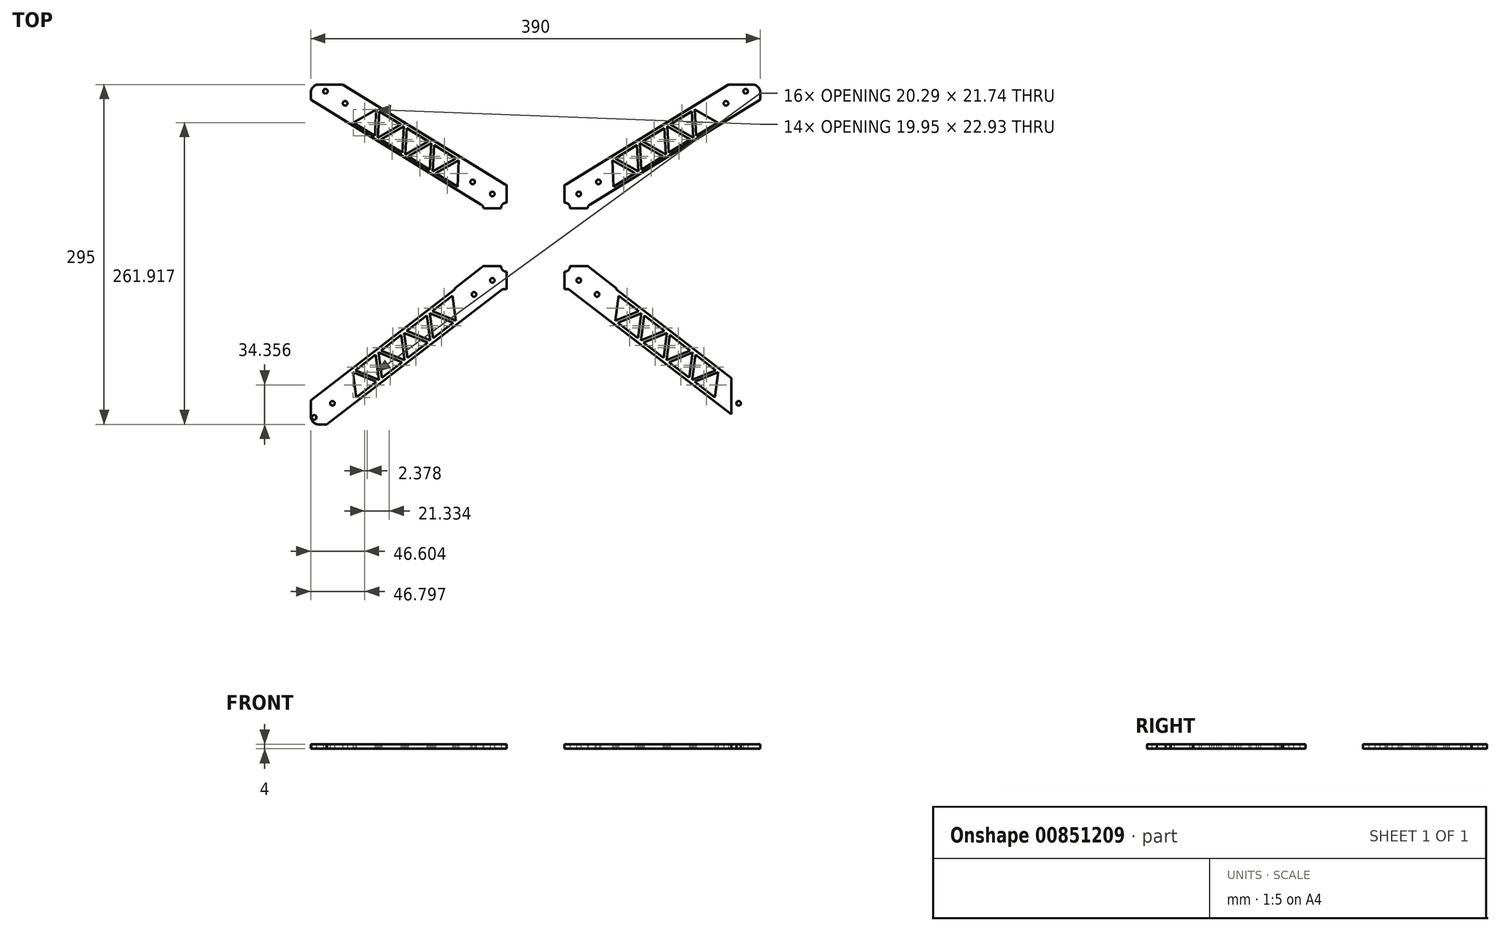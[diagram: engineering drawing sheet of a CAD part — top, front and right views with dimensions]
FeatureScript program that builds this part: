
annotation { "Feature Type Name" : "Feature", "Feature Type Description" : "" }
export const myFeature = defineFeature(function(context is Context, id is Id, definition is map)
    precondition{}
    {
        {
            var Q0;
            Q0=qCreatedBy(makeId("Top.planeOp"),FACE);
            var sketch = newSketch(context, id + "F0", { "sketchPlane" : qUnion([Q0])});
            skLineSegment(sketch, "E0.bottom", {"start": v(-37.5, -37.5) * mm, "end": v(37.5, -37.5) * mm, "construction": true});
            skLineSegment(sketch, "E0.top", {"start": v(-37.5, 37.5) * mm, "end": v(37.5, 37.5) * mm, "construction": true});
            skLineSegment(sketch, "E0.left", {"start": v(-37.5, -37.5) * mm, "end": v(-37.5, 37.5) * mm, "construction": true});
            skLineSegment(sketch, "E0.right", {"start": v(37.5, -37.5) * mm, "end": v(37.5, 37.5) * mm, "construction": true});
            skPoint(sketch, "E0.middle", {"position": v(0, 0) * mm});
            skCircle(sketch, "E1", {"center": v(-37.5, 37.5) * mm, "radius": 2 * mm});
            skCircle(sketch, "E2", {"center": v(37.5, 37.5) * mm, "radius": 2 * mm});
            skCircle(sketch, "E3", {"center": v(37.5, -37.5) * mm, "radius": 2 * mm});
            skCircle(sketch, "E4", {"center": v(-37.5, -37.5) * mm, "radius": 2 * mm});
            skLineSegment(sketch, "E5.bottom", {"start": v(25, -30) * mm, "end": v(-25, -30) * mm});
            skLineSegment(sketch, "E5.top", {"start": v(25, 30) * mm, "end": v(-25, 30) * mm});
            skLineSegment(sketch, "E5.left", {"start": v(30, -25) * mm, "end": v(30, 25) * mm});
            skLineSegment(sketch, "E5.right", {"start": v(-30, -25) * mm, "end": v(-30, 25) * mm});
            skLineSegment(sketch, "E6.bottom", {"start": v(-23.58, 45) * mm, "end": v(-7.48, 45) * mm});
            skLineSegment(sketch, "E6.left", {"start": v(-45, 24.13) * mm, "end": v(-45, -22.54) * mm});
            skLineSegment(sketch, "E6.right", {"start": v(45, 40) * mm, "end": v(45, -40) * mm});
            skPoint(sketch, "E7.visualSharp", {"position": v(-30, 30) * mm});
            skArc(sketch, "E7.filletArc", {"start": v(-25, 30) * mm, "mid": v(-28.54, 28.54) * mm, "end": v(-30, 25) * mm});
            skPoint(sketch, "E8.visualSharp", {"position": v(30, 30) * mm});
            skArc(sketch, "E8.filletArc", {"start": v(30, 25) * mm, "mid": v(28.54, 28.54) * mm, "end": v(25, 30) * mm});
            skPoint(sketch, "E9.visualSharp", {"position": v(30, -30) * mm});
            skArc(sketch, "E9.filletArc", {"start": v(25, -30) * mm, "mid": v(28.54, -28.54) * mm, "end": v(30, -25) * mm});
            skPoint(sketch, "E10.visualSharp", {"position": v(-30, -30) * mm});
            skArc(sketch, "E10.filletArc", {"start": v(-30, -25) * mm, "mid": v(-28.54, -28.54) * mm, "end": v(-25, -30) * mm});
            skPoint(sketch, "E11.visualSharp", {"position": v(45, 45) * mm});
            skArc(sketch, "E11.filletArc", {"start": v(45, 40) * mm, "mid": v(43.54, 43.54) * mm, "end": v(40, 45) * mm});
            skPoint(sketch, "E12.visualSharp", {"position": v(-45, 45) * mm});
            skPoint(sketch, "E13.visualSharp", {"position": v(45, -45) * mm});
            skArc(sketch, "E13.filletArc", {"start": v(40, -45) * mm, "mid": v(43.54, -43.54) * mm, "end": v(45, -40) * mm});
            skPoint(sketch, "E14.visualSharp", {"position": v(-45, -45) * mm});
            skLineSegment(sketch, "E15", {"start": v(-37.5, -37.5) * mm, "end": v(-37.5, -162.5) * mm, "construction": true});
            skLineSegment(sketch, "E16", {"start": v(0, 0) * mm, "end": v(0, -162.5) * mm, "construction": true});
            skLineSegment(sketch, "E17", {"start": v(0, -162.5) * mm, "end": v(200, -162.5) * mm});
            skLineSegment(sketch, "E18", {"start": v(200, -162.5) * mm, "end": v(200, 137.5) * mm, "construction": true});
            skLineSegment(sketch, "E19", {"start": v(200, 137.5) * mm, "end": v(-200, 137.5) * mm, "construction": true});
            skLineSegment(sketch, "E20", {"start": v(-200, 137.5) * mm, "end": v(-200, -162.5) * mm, "construction": true});
            skLineSegment(sketch, "E21", {"start": v(-200, -162.5) * mm, "end": v(0, -162.5) * mm, "construction": true});
            skLineSegment(sketch, "E22", {"start": v(-37.5, 37.5) * mm, "end": v(-200, 137.5) * mm, "construction": true});
            skLineSegment(sketch, "E23", {"start": v(-26.2, 45.74) * mm, "end": v(-56.68, 64.5) * mm});
            skLineSegment(sketch, "E24", {"start": v(-56.68, 64.5) * mm, "end": v(-63.46, 53.47) * mm});
            skLineSegment(sketch, "E25.MirrorCS", {"start": v(-47.38, 28.39) * mm, "end": v(-70.24, 42.45) * mm});
            skLineSegment(sketch, "E26.MirrorCS", {"start": v(-70.24, 42.45) * mm, "end": v(-63.46, 53.47) * mm});
            skPoint(sketch, "E27.orphan", {"position": v(-38.56, 22.96) * mm});
            skPoint(sketch, "E28.visualSharp", {"position": v(-45, 26.92) * mm});
            skArc(sketch, "E28.filletArc", {"start": v(-45, 24.13) * mm, "mid": v(-45.64, 26.57) * mm, "end": v(-47.38, 28.39) * mm});
            skPoint(sketch, "E29.visualSharp", {"position": v(-25, 45) * mm});
            skArc(sketch, "E29.filletArc", {"start": v(-26.2, 45.74) * mm, "mid": v(-24.95, 45.19) * mm, "end": v(-23.58, 45) * mm});
            skLineSegment(sketch, "E30", {"start": v(-37.5, 37.5) * mm, "end": v(-39.84, 33.7) * mm, "construction": true});
            skLineSegment(sketch, "E31", {"start": v(-39.84, 33.7) * mm, "end": v(-56.88, 44.17) * mm, "construction": true});
            skLineSegment(sketch, "E32", {"start": v(-56.88, 44.17) * mm, "end": v(-54.53, 47.98) * mm, "construction": true});
            skCircle(sketch, "E33", {"center": v(-54.53, 47.98) * mm, "radius": 2 * mm});
            skLineSegment(sketch, "E34.bottom", {"start": v(-200, 137.5) * mm, "end": v(-151.5, 137.5) * mm});
            skLineSegment(sketch, "E34.top", {"start": v(-200, 107.5) * mm, "end": v(-151.5, 107.5) * mm});
            skLineSegment(sketch, "E34.left", {"start": v(-200, 137.5) * mm, "end": v(-200, 107.5) * mm});
            skLineSegment(sketch, "E34.right", {"start": v(-151.5, 137.5) * mm, "end": v(-151.5, 107.5) * mm});
            skLineSegment(sketch, "E35.bottom", {"start": v(-151.5, 107.5) * mm, "end": v(-195, 107.5) * mm});
            skLineSegment(sketch, "E35.top", {"start": v(-151.5, 132.5) * mm, "end": v(-195, 132.5) * mm});
            skLineSegment(sketch, "E35.left", {"start": v(-151.5, 107.5) * mm, "end": v(-151.5, 132.5) * mm});
            skLineSegment(sketch, "E35.right", {"start": v(-195, 107.5) * mm, "end": v(-195, 132.5) * mm});
            skLineSegment(sketch, "E36", {"start": v(-56.88, 44.17) * mm, "end": v(-167.6, 112.3) * mm, "construction": true});
            skLineSegment(sketch, "E37", {"start": v(-167.6, 112.3) * mm, "end": v(-165.25, 116.11) * mm, "construction": true});
            skCircle(sketch, "E38", {"center": v(-165.25, 116.11) * mm, "radius": 2 * mm});
            skLineSegment(sketch, "E39", {"start": v(-167.6, 112.3) * mm, "end": v(-184.63, 122.79) * mm, "construction": true});
            skLineSegment(sketch, "E40", {"start": v(-184.63, 122.79) * mm, "end": v(-182.28, 126.6) * mm, "construction": true});
            skCircle(sketch, "E41", {"center": v(-182.28, 126.6) * mm, "radius": 2 * mm});
            skLineSegment(sketch, "E42", {"start": v(0, -34.68) * mm, "end": v(15, -34.68) * mm, "construction": true});
            skCircle(sketch, "E43", {"center": v(15, -37.5) * mm, "radius": 2.2 * mm});
            skLineSegment(sketch, "E44", {"start": v(0, 0) * mm, "end": v(-16.78, 0) * mm, "construction": true});
            skLineSegment(sketch, "E45", {"start": v(0, 0) * mm, "end": v(-10.77, -10.77) * mm, "construction": true});
            skCircle(sketch, "E46.MirrorC", {"center": v(-15, -37.5) * mm, "radius": 2.2 * mm});
            skCircle(sketch, "E47.MirrorC", {"center": v(-37.5, 15) * mm, "radius": 2.2 * mm});
            skCircle(sketch, "E48.MirrorC", {"center": v(-37.5, -15) * mm, "radius": 2.2 * mm});
            skCircle(sketch, "E49.MirrorC", {"center": v(-15, 37.5) * mm, "radius": 2.2 * mm});
            skCircle(sketch, "E50.MirrorC", {"center": v(15, 37.5) * mm, "radius": 2.2 * mm});
            skCircle(sketch, "E51.MirrorC", {"center": v(37.5, -15) * mm, "radius": 2.2 * mm});
            skCircle(sketch, "E52.MirrorC", {"center": v(37.5, 15) * mm, "radius": 2.2 * mm});
            skLineSegment(sketch, "E53", {"start": v(0, 0) * mm, "end": v(-200, 0) * mm, "construction": true});
            skLineSegment(sketch, "E54", {"start": v(0, 0) * mm, "end": v(0, 137.5) * mm, "construction": true});
            skLineSegment(sketch, "E55.MirrorCS", {"start": v(167.6, 112.3) * mm, "end": v(165.25, 116.11) * mm, "construction": true});
            skCircle(sketch, "E56.MirrorC", {"center": v(165.25, 116.11) * mm, "radius": 2 * mm});
            skCircle(sketch, "E57.MirrorC", {"center": v(182.28, 126.6) * mm, "radius": 2 * mm});
            skLineSegment(sketch, "E58.MirrorCS", {"start": v(184.63, 122.79) * mm, "end": v(182.28, 126.6) * mm, "construction": true});
            skLineSegment(sketch, "E59.MirrorCS", {"start": v(151.5, 107.5) * mm, "end": v(151.5, 132.5) * mm});
            skLineSegment(sketch, "E60.MirrorCS", {"start": v(151.5, 107.5) * mm, "end": v(195, 107.5) * mm});
            skLineSegment(sketch, "E61.MirrorCS", {"start": v(151.5, 132.5) * mm, "end": v(195, 132.5) * mm});
            skLineSegment(sketch, "E62.MirrorCS", {"start": v(200, 137.5) * mm, "end": v(151.5, 137.5) * mm});
            skLineSegment(sketch, "E63.MirrorCS", {"start": v(151.5, 137.5) * mm, "end": v(151.5, 107.5) * mm});
            skLineSegment(sketch, "E64.MirrorCS", {"start": v(195, 107.5) * mm, "end": v(195, 132.5) * mm});
            skLineSegment(sketch, "E65.MirrorCS", {"start": v(167.6, 112.3) * mm, "end": v(184.63, 122.79) * mm, "construction": true});
            skLineSegment(sketch, "E66.MirrorCS", {"start": v(200, 107.5) * mm, "end": v(151.5, 107.5) * mm});
            skLineSegment(sketch, "E67.MirrorCS", {"start": v(200, 137.5) * mm, "end": v(200, 107.5) * mm});
            skLineSegment(sketch, "E68", {"start": v(-37.5, -37.5) * mm, "end": v(-200, -162.5) * mm, "construction": true});
            skLineSegment(sketch, "E69.bottom", {"start": v(-200, -162.5) * mm, "end": v(-170, -162.5) * mm});
            skLineSegment(sketch, "E69.top", {"start": v(-200, -114) * mm, "end": v(-170, -114) * mm});
            skLineSegment(sketch, "E69.left", {"start": v(-200, -162.5) * mm, "end": v(-200, -114) * mm});
            skLineSegment(sketch, "E69.right", {"start": v(-170, -162.5) * mm, "end": v(-170, -114) * mm});
            skLineSegment(sketch, "E70", {"start": v(-46.95, -26.5) * mm, "end": v(-70.24, -44.42) * mm});
            skLineSegment(sketch, "E71", {"start": v(-70.24, 42.45) * mm, "end": v(-70.24, -45.57) * mm, "construction": true});
            skLineSegment(sketch, "E72", {"start": v(-70.24, -44.42) * mm, "end": v(-54.47, -64.92) * mm});
            skLineSegment(sketch, "E73", {"start": v(-54.47, -64.92) * mm, "end": v(-29.92, -46.04) * mm});
            skLineSegment(sketch, "E74", {"start": v(-37.5, -37.5) * mm, "end": v(-40.46, -33.65) * mm, "construction": true});
            skLineSegment(sketch, "E75", {"start": v(-40.46, -33.65) * mm, "end": v(-56.31, -45.85) * mm, "construction": true});
            skLineSegment(sketch, "E76", {"start": v(-56.31, -45.85) * mm, "end": v(-53.35, -49.7) * mm, "construction": true});
            skCircle(sketch, "E77", {"center": v(-53.35, -49.7) * mm, "radius": 2 * mm});
            skLineSegment(sketch, "E78", {"start": v(-56.31, -45.85) * mm, "end": v(-179.17, -140.35) * mm, "construction": true});
            skLineSegment(sketch, "E79", {"start": v(-179.17, -140.35) * mm, "end": v(-176.2, -144.2) * mm, "construction": true});
            skCircle(sketch, "E80", {"center": v(-176.2, -144.2) * mm, "radius": 2 * mm});
            skLineSegment(sketch, "E81", {"start": v(-179.17, -140.35) * mm, "end": v(-195.02, -152.55) * mm, "construction": true});
            skLineSegment(sketch, "E82", {"start": v(-195.02, -152.55) * mm, "end": v(-192.06, -156.4) * mm, "construction": true});
            skCircle(sketch, "E83", {"center": v(-192.06, -156.4) * mm, "radius": 2 * mm});
            skLineSegment(sketch, "E84.bottom", {"start": v(-170, -114) * mm, "end": v(-195, -114) * mm});
            skLineSegment(sketch, "E84.top", {"start": v(-170, -162.5) * mm, "end": v(-195, -162.5) * mm});
            skLineSegment(sketch, "E84.left", {"start": v(-170, -114) * mm, "end": v(-170, -162.5) * mm});
            skLineSegment(sketch, "E84.right", {"start": v(-195, -114) * mm, "end": v(-195, -162.5) * mm});
            skLineSegment(sketch, "E85.MirrorCS", {"start": v(179.17, -140.35) * mm, "end": v(176.2, -144.2) * mm, "construction": true});
            skCircle(sketch, "E86.MirrorC", {"center": v(176.2, -144.2) * mm, "radius": 2 * mm});
            skCircle(sketch, "E87.MirrorC", {"center": v(192.06, -156.4) * mm, "radius": 2 * mm});
            skLineSegment(sketch, "E88.MirrorCS", {"start": v(195.02, -152.55) * mm, "end": v(192.06, -156.4) * mm, "construction": true});
            skLineSegment(sketch, "E89.MirrorCS", {"start": v(170, -162.5) * mm, "end": v(170, -114) * mm});
            skLineSegment(sketch, "E90.MirrorCS", {"start": v(179.17, -140.35) * mm, "end": v(195.02, -152.55) * mm, "construction": true});
            skLineSegment(sketch, "E91.MirrorCS", {"start": v(170, -162.5) * mm, "end": v(195, -162.5) * mm});
            skLineSegment(sketch, "E92.MirrorCS", {"start": v(200, -114) * mm, "end": v(170, -114) * mm});
            skLineSegment(sketch, "E93.MirrorCS", {"start": v(170, -114) * mm, "end": v(195, -114) * mm});
            skLineSegment(sketch, "E94.MirrorCS", {"start": v(200, -162.5) * mm, "end": v(200, -114) * mm});
            skLineSegment(sketch, "E95.MirrorCS", {"start": v(170, -114) * mm, "end": v(170, -162.5) * mm});
            skLineSegment(sketch, "E96.MirrorCS", {"start": v(200, -162.5) * mm, "end": v(170, -162.5) * mm});
            skLineSegment(sketch, "E97.MirrorCS", {"start": v(195, -114) * mm, "end": v(195, -162.5) * mm});
            skLineSegment(sketch, "E98.trimOffspring", {"start": v(-26.87, -45) * mm, "end": v(40, -45) * mm});
            skPoint(sketch, "E99.visualSharp", {"position": v(-45, -25) * mm});
            skArc(sketch, "E99.filletArc", {"start": v(-46.95, -26.5) * mm, "mid": v(-45.51, -24.75) * mm, "end": v(-45, -22.54) * mm});
            skPoint(sketch, "E100.visualSharp", {"position": v(-28.57, -45) * mm});
            skArc(sketch, "E100.filletArc", {"start": v(-26.87, -45) * mm, "mid": v(-28.48, -45.27) * mm, "end": v(-29.92, -46.04) * mm});
            skPoint(sketch, "E101.MirrorP", {"position": v(28.57, -45) * mm});
            skArc(sketch, "E102.MirrorCS", {"start": v(26.87, -45) * mm, "mid": v(28.48, -45.27) * mm, "end": v(29.92, -46.04) * mm});
            skLineSegment(sketch, "E103.MirrorCS", {"start": v(54.47, -64.92) * mm, "end": v(29.92, -46.04) * mm});
            skArc(sketch, "E104.MirrorCS", {"start": v(46.95, -26.5) * mm, "mid": v(45.51, -24.75) * mm, "end": v(45, -22.54) * mm});
            skLineSegment(sketch, "E105.MirrorCS", {"start": v(46.95, -26.5) * mm, "end": v(70.24, -44.42) * mm});
            skCircle(sketch, "E106.MirrorC", {"center": v(53.35, -49.7) * mm, "radius": 2 * mm});
            skLineSegment(sketch, "E107.MirrorCS", {"start": v(70.24, -44.42) * mm, "end": v(54.47, -64.92) * mm});
            skArc(sketch, "E108.MirrorCS", {"start": v(26.2, 45.74) * mm, "mid": v(24.95, 45.19) * mm, "end": v(23.58, 45) * mm});
            skLineSegment(sketch, "E109.MirrorCS", {"start": v(26.2, 45.74) * mm, "end": v(56.68, 64.5) * mm});
            skArc(sketch, "E110.MirrorCS", {"start": v(45, 24.13) * mm, "mid": v(45.64, 26.57) * mm, "end": v(47.38, 28.39) * mm});
            skLineSegment(sketch, "E111.MirrorCS", {"start": v(47.38, 28.39) * mm, "end": v(70.24, 42.45) * mm});
            skLineSegment(sketch, "E112.MirrorCS", {"start": v(56.68, 64.5) * mm, "end": v(63.46, 53.47) * mm});
            skCircle(sketch, "E113.MirrorC", {"center": v(54.53, 47.98) * mm, "radius": 2 * mm});
            skLineSegment(sketch, "E114.MirrorCS", {"start": v(70.24, 42.45) * mm, "end": v(63.46, 53.47) * mm});
            skArc(sketch, "E115", {"start": v(3.33, 47.22) * mm, "mid": v(0, 49) * mm, "end": v(-3.33, 47.22) * mm});
            skLineSegment(sketch, "E116.trimOffspring", {"start": v(7.48, 45) * mm, "end": v(40, 45) * mm});
            skPoint(sketch, "E117.visualSharp", {"position": v(4, 45) * mm});
            skArc(sketch, "E117.filletArc", {"start": v(3.33, 47.22) * mm, "mid": v(5.13, 45.6) * mm, "end": v(7.48, 45) * mm});
            skPoint(sketch, "E118.visualSharp", {"position": v(-4, 45) * mm});
            skArc(sketch, "E118.filletArc", {"start": v(-7.48, 45) * mm, "mid": v(-5.13, 45.6) * mm, "end": v(-3.33, 47.22) * mm});
            skLineSegment(sketch, "E119", {"start": v(-165.25, 116.11) * mm, "end": v(-161.58, 122.08) * mm, "construction": true});
            skLineSegment(sketch, "E120", {"start": v(-161.58, 122.08) * mm, "end": v(-151.5, 115.87) * mm});
            skLineSegment(sketch, "E121", {"start": v(-161.58, 122.08) * mm, "end": v(-178.52, 132.5) * mm});
            skLineSegment(sketch, "E122.MirrorCS", {"start": v(-30.16, 49.42) * mm, "end": v(-192.66, 149.42) * mm, "construction": true});
            skLineSegment(sketch, "E123.MirrorCS", {"start": v(-168.92, 110.15) * mm, "end": v(-185.86, 120.58) * mm});
            skLineSegment(sketch, "E124", {"start": v(-168.92, 110.15) * mm, "end": v(-164.6, 107.5) * mm});
            skLineSegment(sketch, "E125", {"start": v(-185.86, 120.58) * mm, "end": v(-195, 126.2) * mm});
            skLineSegment(sketch, "E126", {"start": v(-164.6, 107.5) * mm, "end": v(-157.27, 119.42) * mm});
            skLineSegment(sketch, "E127", {"start": v(-70.24, 42.45) * mm, "end": v(-195, 119.23) * mm});
            skLineSegment(sketch, "E128", {"start": v(-56.68, 64.5) * mm, "end": v(-167.19, 132.5) * mm});
            skLineSegment(sketch, "E129", {"start": v(-30, 25) * mm, "end": v(-45.08, 25) * mm});
            skLineSegment(sketch, "E130", {"start": v(-25, 30) * mm, "end": v(-25, 45.2) * mm});
            skLineSegment(sketch, "E131", {"start": v(-159.49, 97.38) * mm, "end": v(-158.18, 99.5) * mm, "construction": true});
            skLineSegment(sketch, "E132", {"start": v(-158.18, 99.5) * mm, "end": v(-139.4, 87.95) * mm});
            skLineSegment(sketch, "E133", {"start": v(-148.79, 93.73) * mm, "end": v(-138.23, 110.88) * mm, "construction": true});
            skLineSegment(sketch, "E134", {"start": v(-139.4, 87.95) * mm, "end": v(-138.23, 110.88) * mm});
            skLineSegment(sketch, "E135", {"start": v(-138.23, 110.88) * mm, "end": v(-158.18, 99.5) * mm});
            skLineSegment(sketch, "E136", {"start": v(-139.4, 87.95) * mm, "end": v(-136.84, 86.38) * mm, "construction": true});
            skLineSegment(sketch, "E137", {"start": v(-138.23, 110.88) * mm, "end": v(-135.67, 109.31) * mm, "construction": true});
            skLineSegment(sketch, "E138", {"start": v(-136.84, 86.38) * mm, "end": v(-135.67, 109.31) * mm});
            skLineSegment(sketch, "E139", {"start": v(-135.67, 109.31) * mm, "end": v(-116.9, 97.76) * mm});
            skLineSegment(sketch, "E140", {"start": v(-136.84, 86.38) * mm, "end": v(-116.9, 97.76) * mm});
            skLineSegment(sketch, "E141", {"start": v(-116.9, 97.76) * mm, "end": v(-114.34, 96.18) * mm, "construction": true});
            skLineSegment(sketch, "E142", {"start": v(-114.34, 96.18) * mm, "end": v(-116.1, 93.32) * mm, "construction": true});
            skLineSegment(sketch, "E143.MirrorCS", {"start": v(-112.95, 71.68) * mm, "end": v(-111.79, 94.61) * mm});
            skLineSegment(sketch, "E144.MirrorCS", {"start": v(-93, 83.05) * mm, "end": v(-111.79, 94.61) * mm});
            skLineSegment(sketch, "E145.MirrorCS", {"start": v(-112.95, 71.68) * mm, "end": v(-93, 83.05) * mm});
            skLineSegment(sketch, "E146.MirrorCS", {"start": v(-110.4, 70.1) * mm, "end": v(-90.45, 81.48) * mm});
            skLineSegment(sketch, "E147.MirrorCS", {"start": v(-91.62, 58.55) * mm, "end": v(-110.4, 70.1) * mm});
            skLineSegment(sketch, "E148.MirrorCS", {"start": v(-90.45, 81.48) * mm, "end": v(-91.62, 58.55) * mm});
            skLineSegment(sketch, "E149", {"start": v(-138.12, 87.16) * mm, "end": v(-138.8, 86.07) * mm, "construction": true});
            skLineSegment(sketch, "E150", {"start": v(-136.84, 86.38) * mm, "end": v(-139.31, 82.36) * mm, "construction": true});
            skLineSegment(sketch, "E151.MirrorCS", {"start": v(-134.29, 84.8) * mm, "end": v(-114.34, 96.18) * mm});
            skLineSegment(sketch, "E152.MirrorCS", {"start": v(-114.34, 96.18) * mm, "end": v(-115.5, 73.25) * mm});
            skLineSegment(sketch, "E153.MirrorCS", {"start": v(-115.5, 73.25) * mm, "end": v(-134.29, 84.8) * mm});
            skLineSegment(sketch, "E154", {"start": v(-101, 64.33) * mm, "end": v(-103.36, 60.5) * mm, "construction": true});
            skLineSegment(sketch, "E155.MirrorCS", {"start": v(-89.06, 56.97) * mm, "end": v(-69.12, 68.35) * mm});
            skLineSegment(sketch, "E156.MirrorCS", {"start": v(-89.06, 56.97) * mm, "end": v(-87.9, 79.9) * mm});
            skLineSegment(sketch, "E157.MirrorCS", {"start": v(-87.9, 79.9) * mm, "end": v(-69.12, 68.35) * mm});
            skLineSegment(sketch, "E158", {"start": v(-89.06, 56.97) * mm, "end": v(-91.75, 52.6) * mm, "construction": true});
            skLineSegment(sketch, "E159.MirrorCS", {"start": v(-66.56, 66.78) * mm, "end": v(-86.5, 55.4) * mm});
            skLineSegment(sketch, "E160.MirrorCS", {"start": v(-67.73, 43.85) * mm, "end": v(-66.56, 66.78) * mm});
            skLineSegment(sketch, "E161.MirrorCS", {"start": v(-86.5, 55.4) * mm, "end": v(-67.73, 43.85) * mm});
            skLineSegment(sketch, "E162", {"start": v(-54.47, -64.92) * mm, "end": v(-190.45, -169.52) * mm});
            skLineSegment(sketch, "E163", {"start": v(-70.24, -45.57) * mm, "end": v(-195, -141.54) * mm});
            skPoint(sketch, "E163.endSnap0", {"position": v(-195, -138.25) * mm});
            skLineSegment(sketch, "E164", {"start": v(-73.84, -48.34) * mm, "end": v(-72.01, -50.71) * mm, "construction": true});
            skLineSegment(sketch, "E165", {"start": v(-72.01, -50.71) * mm, "end": v(-89.48, -64.15) * mm});
            skLineSegment(sketch, "E166", {"start": v(-80.75, -57.43) * mm, "end": v(-69.2, -72.45) * mm, "construction": true});
            skLineSegment(sketch, "E167", {"start": v(-72.01, -50.71) * mm, "end": v(-69.2, -72.45) * mm});
            skLineSegment(sketch, "E168", {"start": v(-89.48, -64.15) * mm, "end": v(-69.2, -72.45) * mm});
            skLineSegment(sketch, "E169", {"start": v(-89.48, -64.15) * mm, "end": v(-91.86, -65.98) * mm, "construction": true});
            skLineSegment(sketch, "E170", {"start": v(-69.2, -72.45) * mm, "end": v(-71.57, -74.28) * mm, "construction": true});
            skLineSegment(sketch, "E171", {"start": v(-91.86, -65.98) * mm, "end": v(-71.57, -74.28) * mm});
            skLineSegment(sketch, "E172", {"start": v(-71.57, -74.28) * mm, "end": v(-89.04, -87.72) * mm});
            skLineSegment(sketch, "E173", {"start": v(-91.86, -65.98) * mm, "end": v(-89.04, -87.72) * mm});
            skLineSegment(sketch, "E174", {"start": v(-80.3, -81) * mm, "end": v(-78.47, -83.39) * mm, "construction": true});
            skLineSegment(sketch, "E175.MirrorCS", {"start": v(-94.24, -67.81) * mm, "end": v(-91.42, -89.55) * mm});
            skLineSegment(sketch, "E176.MirrorCS", {"start": v(-111.7, -81.25) * mm, "end": v(-94.24, -67.81) * mm});
            skLineSegment(sketch, "E177.MirrorCS", {"start": v(-111.7, -81.25) * mm, "end": v(-91.42, -89.55) * mm});
            skLineSegment(sketch, "E178", {"start": v(-91.42, -89.55) * mm, "end": v(-89.59, -91.94) * mm, "construction": true});
            skLineSegment(sketch, "E179.MirrorCS", {"start": v(-114.09, -83.08) * mm, "end": v(-93.8, -91.38) * mm});
            skLineSegment(sketch, "E180.MirrorCS", {"start": v(-111.27, -104.82) * mm, "end": v(-93.8, -91.38) * mm});
            skLineSegment(sketch, "E181.MirrorCS", {"start": v(-114.09, -83.08) * mm, "end": v(-111.27, -104.82) * mm});
            skLineSegment(sketch, "E182", {"start": v(-102.53, -98.1) * mm, "end": v(-100.7, -100.48) * mm, "construction": true});
            skLineSegment(sketch, "E183.MirrorCS", {"start": v(-116.46, -84.9) * mm, "end": v(-113.65, -106.65) * mm});
            skLineSegment(sketch, "E184.MirrorCS", {"start": v(-133.94, -98.35) * mm, "end": v(-113.65, -106.65) * mm});
            skLineSegment(sketch, "E185.MirrorCS", {"start": v(-116.46, -84.9) * mm, "end": v(-133.94, -98.35) * mm});
            skLineSegment(sketch, "E186.MirrorCS", {"start": v(-136.31, -100.18) * mm, "end": v(-116.03, -108.48) * mm});
            skLineSegment(sketch, "E187.MirrorCS", {"start": v(-133.5, -121.92) * mm, "end": v(-116.03, -108.48) * mm});
            skLineSegment(sketch, "E188.MirrorCS", {"start": v(-136.31, -100.18) * mm, "end": v(-133.5, -121.92) * mm});
            skLineSegment(sketch, "E189.MirrorCS", {"start": v(-138.7, -102) * mm, "end": v(-135.87, -123.74) * mm});
            skLineSegment(sketch, "E190.MirrorCS", {"start": v(-156.16, -115.45) * mm, "end": v(-138.7, -102) * mm});
            skLineSegment(sketch, "E191.MirrorCS", {"start": v(-156.16, -115.45) * mm, "end": v(-135.87, -123.74) * mm});
            skLineSegment(sketch, "E192", {"start": v(-135.87, -123.74) * mm, "end": v(-134.04, -126.13) * mm, "construction": true});
            skLineSegment(sketch, "E193.MirrorCS", {"start": v(-138.25, -125.57) * mm, "end": v(-155.72, -139.01) * mm});
            skLineSegment(sketch, "E194.MirrorCS", {"start": v(-158.54, -117.27) * mm, "end": v(-138.25, -125.57) * mm});
            skLineSegment(sketch, "E195.MirrorCS", {"start": v(-158.54, -117.27) * mm, "end": v(-155.72, -139.01) * mm});
            skLineSegment(sketch, "E196", {"start": v(-30, -25) * mm, "end": v(-45.65, -25) * mm});
            skLineSegment(sketch, "E197", {"start": v(-25, -30) * mm, "end": v(-25, -45) * mm});
            skLineSegment(sketch, "E198", {"start": v(-70.24, -44.42) * mm, "end": v(-70.24, -45.57) * mm});
            skLineSegment(sketch, "E199.MirrorCS", {"start": v(37.5, -37.5) * mm, "end": v(40.46, -33.65) * mm, "construction": true});
            skLineSegment(sketch, "E200.MirrorCS", {"start": v(37.5, 37.5) * mm, "end": v(39.84, 33.7) * mm, "construction": true});
            skLineSegment(sketch, "E201.MirrorCS", {"start": v(168.92, 110.15) * mm, "end": v(164.6, 107.5) * mm});
            skLineSegment(sketch, "E202.MirrorCS", {"start": v(138.12, 87.16) * mm, "end": v(138.8, 86.07) * mm, "construction": true});
            skLineSegment(sketch, "E203.MirrorCS", {"start": v(136.84, 86.38) * mm, "end": v(139.31, 82.36) * mm, "construction": true});
            skLineSegment(sketch, "E204.MirrorCS", {"start": v(138.23, 110.88) * mm, "end": v(135.67, 109.31) * mm, "construction": true});
            skLineSegment(sketch, "E205.MirrorCS", {"start": v(139.4, 87.95) * mm, "end": v(136.84, 86.38) * mm, "construction": true});
            skLineSegment(sketch, "E206.MirrorCS", {"start": v(89.48, -64.15) * mm, "end": v(91.86, -65.98) * mm, "construction": true});
            skLineSegment(sketch, "E207.MirrorCS", {"start": v(116.9, 97.76) * mm, "end": v(114.34, 96.18) * mm, "construction": true});
            skLineSegment(sketch, "E208.MirrorCS", {"start": v(30, 25) * mm, "end": v(45.08, 25) * mm});
            skLineSegment(sketch, "E209.MirrorCS", {"start": v(69.2, -72.45) * mm, "end": v(71.57, -74.28) * mm, "construction": true});
            skLineSegment(sketch, "E210.MirrorCS", {"start": v(164.6, 107.5) * mm, "end": v(157.27, 119.42) * mm});
            skLineSegment(sketch, "E211.MirrorCS", {"start": v(138.23, 110.88) * mm, "end": v(158.18, 99.5) * mm});
            skLineSegment(sketch, "E212.MirrorCS", {"start": v(114.34, 96.18) * mm, "end": v(116.1, 93.32) * mm, "construction": true});
            skLineSegment(sketch, "E213.MirrorCS", {"start": v(25, 30) * mm, "end": v(25, 45.2) * mm});
            skLineSegment(sketch, "E214.MirrorCS", {"start": v(159.49, 97.38) * mm, "end": v(158.18, 99.5) * mm, "construction": true});
            skLineSegment(sketch, "E215.MirrorCS", {"start": v(165.25, 116.11) * mm, "end": v(161.58, 122.08) * mm, "construction": true});
            skLineSegment(sketch, "E216.MirrorCS", {"start": v(73.84, -48.34) * mm, "end": v(72.01, -50.71) * mm, "construction": true});
            skLineSegment(sketch, "E217.MirrorCS", {"start": v(70.24, -44.42) * mm, "end": v(70.24, -45.57) * mm});
            skArc(sketch, "E218.MirrorCS", {"start": v(30, -25) * mm, "mid": v(28.54, -28.54) * mm, "end": v(25, -30) * mm});
            skArc(sketch, "E219.MirrorCS", {"start": v(25, 30) * mm, "mid": v(28.54, 28.54) * mm, "end": v(30, 25) * mm});
            skLineSegment(sketch, "E220.MirrorCS", {"start": v(56.31, -45.85) * mm, "end": v(53.35, -49.7) * mm, "construction": true});
            skLineSegment(sketch, "E221.MirrorCS", {"start": v(30, -25) * mm, "end": v(45.65, -25) * mm});
            skLineSegment(sketch, "E222.MirrorCS", {"start": v(135.87, -123.74) * mm, "end": v(134.04, -126.13) * mm, "construction": true});
            skLineSegment(sketch, "E223.MirrorCS", {"start": v(89.06, 56.97) * mm, "end": v(91.75, 52.6) * mm, "construction": true});
            skLineSegment(sketch, "E224.MirrorCS", {"start": v(161.58, 122.08) * mm, "end": v(151.5, 115.87) * mm});
            skLineSegment(sketch, "E225.MirrorCS", {"start": v(91.42, -89.55) * mm, "end": v(89.59, -91.94) * mm, "construction": true});
            skLineSegment(sketch, "E226.MirrorCS", {"start": v(25, -30) * mm, "end": v(25, -45) * mm});
            skLineSegment(sketch, "E227.MirrorCS", {"start": v(40.46, -33.65) * mm, "end": v(56.31, -45.85) * mm, "construction": true});
            skLineSegment(sketch, "E228.MirrorCS", {"start": v(56.88, 44.17) * mm, "end": v(54.53, 47.98) * mm, "construction": true});
            skLineSegment(sketch, "E229.MirrorCS", {"start": v(72.01, -50.71) * mm, "end": v(89.48, -64.15) * mm});
            skLineSegment(sketch, "E230.MirrorCS", {"start": v(67.73, 43.85) * mm, "end": v(66.56, 66.78) * mm});
            skLineSegment(sketch, "E231.MirrorCS", {"start": v(91.62, 58.55) * mm, "end": v(110.4, 70.1) * mm});
            skLineSegment(sketch, "E232.MirrorCS", {"start": v(138.25, -125.57) * mm, "end": v(155.72, -139.01) * mm});
            skLineSegment(sketch, "E233.MirrorCS", {"start": v(136.31, -100.18) * mm, "end": v(133.5, -121.92) * mm});
            skLineSegment(sketch, "E234.MirrorCS", {"start": v(94.24, -67.81) * mm, "end": v(91.42, -89.55) * mm});
            skLineSegment(sketch, "E235.MirrorCS", {"start": v(116.46, -84.9) * mm, "end": v(133.94, -98.35) * mm});
            skLineSegment(sketch, "E236.MirrorCS", {"start": v(116.46, -84.9) * mm, "end": v(113.65, -106.65) * mm});
            skLineSegment(sketch, "E237.MirrorCS", {"start": v(158.18, 99.5) * mm, "end": v(139.4, 87.95) * mm});
            skLineSegment(sketch, "E238.MirrorCS", {"start": v(101, 64.33) * mm, "end": v(103.36, 60.5) * mm, "construction": true});
            skLineSegment(sketch, "E239.MirrorCS", {"start": v(91.86, -65.98) * mm, "end": v(89.04, -87.72) * mm});
            skLineSegment(sketch, "E240.MirrorCS", {"start": v(114.09, -83.08) * mm, "end": v(111.27, -104.82) * mm});
            skLineSegment(sketch, "E241.MirrorCS", {"start": v(110.4, 70.1) * mm, "end": v(90.45, 81.48) * mm});
            skLineSegment(sketch, "E242.MirrorCS", {"start": v(71.57, -74.28) * mm, "end": v(89.04, -87.72) * mm});
            skLineSegment(sketch, "E243.MirrorCS", {"start": v(111.27, -104.82) * mm, "end": v(93.8, -91.38) * mm});
            skLineSegment(sketch, "E244.MirrorCS", {"start": v(112.95, 71.68) * mm, "end": v(111.79, 94.61) * mm});
            skLineSegment(sketch, "E245.MirrorCS", {"start": v(72.01, -50.71) * mm, "end": v(69.2, -72.45) * mm});
            skLineSegment(sketch, "E246.MirrorCS", {"start": v(39.84, 33.7) * mm, "end": v(56.88, 44.17) * mm, "construction": true});
            skLineSegment(sketch, "E247.MirrorCS", {"start": v(89.06, 56.97) * mm, "end": v(69.12, 68.35) * mm});
            skLineSegment(sketch, "E248.MirrorCS", {"start": v(134.29, 84.8) * mm, "end": v(114.34, 96.18) * mm});
            skLineSegment(sketch, "E249.MirrorCS", {"start": v(66.56, 66.78) * mm, "end": v(86.5, 55.4) * mm});
            skLineSegment(sketch, "E250.MirrorCS", {"start": v(80.3, -81) * mm, "end": v(78.47, -83.39) * mm, "construction": true});
            skLineSegment(sketch, "E251.MirrorCS", {"start": v(158.54, -117.27) * mm, "end": v(138.25, -125.57) * mm});
            skLineSegment(sketch, "E252.MirrorCS", {"start": v(136.31, -100.18) * mm, "end": v(116.03, -108.48) * mm});
            skLineSegment(sketch, "E253.MirrorCS", {"start": v(90.45, 81.48) * mm, "end": v(91.62, 58.55) * mm});
            skLineSegment(sketch, "E254.MirrorCS", {"start": v(102.53, -98.1) * mm, "end": v(100.7, -100.48) * mm, "construction": true});
            skLineSegment(sketch, "E255.MirrorCS", {"start": v(136.84, 86.38) * mm, "end": v(135.67, 109.31) * mm});
            skLineSegment(sketch, "E256.MirrorCS", {"start": v(161.58, 122.08) * mm, "end": v(178.52, 132.5) * mm});
            skLineSegment(sketch, "E257.MirrorCS", {"start": v(89.06, 56.97) * mm, "end": v(87.9, 79.9) * mm});
            skLineSegment(sketch, "E258.MirrorCS", {"start": v(148.79, 93.73) * mm, "end": v(138.23, 110.88) * mm, "construction": true});
            skLineSegment(sketch, "E259.MirrorCS", {"start": v(114.09, -83.08) * mm, "end": v(93.8, -91.38) * mm});
            skLineSegment(sketch, "E260.MirrorCS", {"start": v(91.86, -65.98) * mm, "end": v(71.57, -74.28) * mm});
            skLineSegment(sketch, "E261.MirrorCS", {"start": v(138.7, -102) * mm, "end": v(135.87, -123.74) * mm});
            skLineSegment(sketch, "E262.MirrorCS", {"start": v(111.7, -81.25) * mm, "end": v(91.42, -89.55) * mm});
            skLineSegment(sketch, "E263.MirrorCS", {"start": v(112.95, 71.68) * mm, "end": v(93, 83.05) * mm});
            skLineSegment(sketch, "E264.MirrorCS", {"start": v(114.34, 96.18) * mm, "end": v(115.5, 73.25) * mm});
            skLineSegment(sketch, "E265.MirrorCS", {"start": v(89.48, -64.15) * mm, "end": v(69.2, -72.45) * mm});
            skLineSegment(sketch, "E266.MirrorCS", {"start": v(156.16, -115.45) * mm, "end": v(135.87, -123.74) * mm});
            skLineSegment(sketch, "E267.MirrorCS", {"start": v(115.5, 73.25) * mm, "end": v(134.29, 84.8) * mm});
            skLineSegment(sketch, "E268.MirrorCS", {"start": v(139.4, 87.95) * mm, "end": v(138.23, 110.88) * mm});
            skLineSegment(sketch, "E269.MirrorCS", {"start": v(80.75, -57.43) * mm, "end": v(69.2, -72.45) * mm, "construction": true});
            skLineSegment(sketch, "E270.MirrorCS", {"start": v(168.92, 110.15) * mm, "end": v(185.86, 120.58) * mm});
            skLineSegment(sketch, "E271.MirrorCS", {"start": v(133.94, -98.35) * mm, "end": v(113.65, -106.65) * mm});
            skLineSegment(sketch, "E272.MirrorCS", {"start": v(158.54, -117.27) * mm, "end": v(155.72, -139.01) * mm});
            skLineSegment(sketch, "E273.MirrorCS", {"start": v(185.86, 120.58) * mm, "end": v(195, 126.2) * mm});
            skLineSegment(sketch, "E274.MirrorCS", {"start": v(56.68, 64.5) * mm, "end": v(167.19, 132.5) * mm});
            skPoint(sketch, "E275.MirrorP", {"position": v(25, 45) * mm});
            skLineSegment(sketch, "E276.MirrorCS", {"start": v(111.7, -81.25) * mm, "end": v(94.24, -67.81) * mm});
            skLineSegment(sketch, "E277.MirrorCS", {"start": v(135.67, 109.31) * mm, "end": v(116.9, 97.76) * mm});
            skPoint(sketch, "E278.MirrorP", {"position": v(45, -25) * mm});
            skLineSegment(sketch, "E279.MirrorCS", {"start": v(45, 24.13) * mm, "end": v(45, -22.54) * mm});
            skLineSegment(sketch, "E280.MirrorCS", {"start": v(56.31, -45.85) * mm, "end": v(179.17, -140.35) * mm, "construction": true});
            skLineSegment(sketch, "E281.MirrorCS", {"start": v(133.5, -121.92) * mm, "end": v(116.03, -108.48) * mm});
            skLineSegment(sketch, "E282.MirrorCS", {"start": v(93, 83.05) * mm, "end": v(111.79, 94.61) * mm});
            skLineSegment(sketch, "E283.MirrorCS", {"start": v(156.16, -115.45) * mm, "end": v(138.7, -102) * mm});
            skLineSegment(sketch, "E284.MirrorCS", {"start": v(37.5, -37.5) * mm, "end": v(37.5, -162.5) * mm, "construction": true});
            skPoint(sketch, "E285.MirrorP", {"position": v(38.56, 22.96) * mm});
            skLineSegment(sketch, "E286.MirrorCS", {"start": v(70.24, 42.45) * mm, "end": v(195, 119.23) * mm});
            skLineSegment(sketch, "E287.MirrorCS", {"start": v(87.9, 79.9) * mm, "end": v(69.12, 68.35) * mm});
            skPoint(sketch, "E288.MirrorP", {"position": v(195, -138.25) * mm});
            skPoint(sketch, "E289.MirrorP", {"position": v(45, 26.92) * mm});
            skLineSegment(sketch, "E290.MirrorCS", {"start": v(37.5, -37.5) * mm, "end": v(200, -162.5) * mm, "construction": true});
            skLineSegment(sketch, "E291.MirrorCS", {"start": v(70.24, 42.45) * mm, "end": v(70.24, -45.57) * mm, "construction": true});
            skLineSegment(sketch, "E292.MirrorCS", {"start": v(56.88, 44.17) * mm, "end": v(167.6, 112.3) * mm, "construction": true});
            skLineSegment(sketch, "E293.MirrorCS", {"start": v(70.24, -45.57) * mm, "end": v(195, -141.54) * mm});
            skLineSegment(sketch, "E294.MirrorCS", {"start": v(30.16, 49.42) * mm, "end": v(192.66, 149.42) * mm, "construction": true});
            skLineSegment(sketch, "E295.MirrorCS", {"start": v(37.5, 37.5) * mm, "end": v(200, 137.5) * mm, "construction": true});
            skLineSegment(sketch, "E296.MirrorCS", {"start": v(54.47, -64.92) * mm, "end": v(190.45, -169.52) * mm});
            skLineSegment(sketch, "E297.MirrorCS", {"start": v(200, 137.5) * mm, "end": v(200, -162.5) * mm, "construction": true});
            skLineSegment(sketch, "E298.MirrorCS", {"start": v(136.84, 86.38) * mm, "end": v(116.9, 97.76) * mm});
            skLineSegment(sketch, "E299.MirrorCS", {"start": v(86.5, 55.4) * mm, "end": v(67.73, 43.85) * mm});
            skSolve(sketch);
        }
        {
            var Q0;
            Q0=makeQuery(id+"F0.imprint","IMPRINT",FACE,{"disambiguationData":[TD([[makeQuery(id+"F0.imprint","IMPRINT",EDGE,{"derivedFrom":sQuery(id+"F0.wireOp",EDGE,"E38")}),-1.0]])]});
            var Q1;
            {var subQ0=sQuery(id+"F0.wireOp",EDGE,"E121");Q1=makeQuery(id+"F0.imprint","IMPRINT",FACE,{"disambiguationData":[TD([[makeQuery(id+"F0.imprint","IMPRINT",EDGE,{"derivedFrom":subQ0}),-1.0]])]});}
            var Q2;
            {var subQ3=sQuery(id+"F0.wireOp",EDGE,"E126");Q2=makeQuery(id+"F0.imprint","IMPRINT",FACE,{"disambiguationData":[TD([[makeQuery(id+"F0.imprint","IMPRINT",EDGE,{"derivedFrom":subQ3}),-1.0]])]});}
            var Q3;
            Q3=makeQuery(id+"F0.imprint","IMPRINT",FACE,{"disambiguationData":[TD([[makeQuery(id+"F0.imprint","IMPRINT",EDGE,{"derivedFrom":sQuery(id+"F0.wireOp",EDGE,"E123.MirrorCS")}),1.0]])]});
            var Q4;
            {var subQ4=sQuery(id+"F0.wireOp",EDGE,"E24");Q4=makeQuery(id+"F0.imprint","IMPRINT",FACE,{"disambiguationData":[TD([[makeQuery(id+"F0.imprint","IMPRINT",EDGE,{"derivedFrom":subQ4}),-1.0]])]});}
            var Q5;
            Q5=makeQuery(id+"F0.imprint","IMPRINT",FACE,{"disambiguationData":[TD([[makeQuery(id+"F0.imprint","IMPRINT",EDGE,{"derivedFrom":sQuery(id+"F0.wireOp",EDGE,"E1")}),-1.0]])]});
            var Q6;
            Q6=makeQuery(id+"F0.imprint","IMPRINT",FACE,{"disambiguationData":[TD([[makeQuery(id+"F0.imprint","IMPRINT",EDGE,{"derivedFrom":sQuery(id+"F0.wireOp",EDGE,"E4")}),-1.0]])]});
            var Q7;
            {var subQ5=sQuery(id+"F0.wireOp",EDGE,"E72");Q7=makeQuery(id+"F0.imprint","IMPRINT",FACE,{"disambiguationData":[TD([[makeQuery(id+"F0.imprint","IMPRINT",EDGE,{"derivedFrom":subQ5}),-1.0]])]});}
            var Q8;
            Q8=makeQuery(id+"F0.imprint","IMPRINT",FACE,{"disambiguationData":[TD([[makeQuery(id+"F0.imprint","IMPRINT",EDGE,{"derivedFrom":sQuery(id+"F0.wireOp",EDGE,"E80")}),-1.0]])]});
            var Q9;
            {var subQ7=sQuery(id+"F0.wireOp",EDGE,"E11.filletArc");Q9=makeQuery(id+"F0.imprint","IMPRINT",FACE,{"disambiguationData":[TD([[makeQuery(id+"F0.imprint","IMPRINT",EDGE,{"derivedFrom":subQ7}),-1.0]])]});}
            var Q10;
            {var subQ0=sQuery(id+"F0.wireOp",EDGE,"E11.filletArc");Q10=makeQuery(id+"F0.imprint","IMPRINT",FACE,{"disambiguationData":[TD([[makeQuery(id+"F0.imprint","IMPRINT",EDGE,{"derivedFrom":subQ0}),1.0]])]});}
            var Q11;
            Q11=makeQuery(id+"F0.imprint","IMPRINT",FACE,{"disambiguationData":[TD([[makeQuery(id+"F0.imprint","IMPRINT",EDGE,{"derivedFrom":sQuery(id+"F0.wireOp",EDGE,"E211.MirrorCS")}),1.0]])]});
            var Q12;
            {var subQ3=sQuery(id+"F0.wireOp",EDGE,"E13.filletArc");Q12=makeQuery(id+"F0.imprint","IMPRINT",FACE,{"disambiguationData":[TD([[makeQuery(id+"F0.imprint","IMPRINT",EDGE,{"derivedFrom":subQ3}),1.0]])]});}
            var Q13;
            {var subQ0=sQuery(id+"F0.wireOp",EDGE,"E13.filletArc");Q13=makeQuery(id+"F0.imprint","IMPRINT",FACE,{"disambiguationData":[TD([[makeQuery(id+"F0.imprint","IMPRINT",EDGE,{"derivedFrom":subQ0}),-1.0]])]});}
            var Q14;
            {var subQ6=sQuery(id+"F0.wireOp",EDGE,"E217.MirrorCS");Q14=makeQuery(id+"F0.imprint","IMPRINT",FACE,{"disambiguationData":[TD([[makeQuery(id+"F0.imprint","IMPRINT",EDGE,{"derivedFrom":subQ6}),-1.0]])]});}
            var Q15;
            {var subQ4=sQuery(id+"F0.wireOp",EDGE,"E256.MirrorCS");Q15=makeQuery(id+"F0.imprint","IMPRINT",FACE,{"disambiguationData":[TD([[makeQuery(id+"F0.imprint","IMPRINT",EDGE,{"derivedFrom":subQ4}),1.0]])]});}
            var Q16;
            {var subQ0=sQuery(id+"F0.wireOp",EDGE,"E210.MirrorCS");Q16=makeQuery(id+"F0.imprint","IMPRINT",FACE,{"disambiguationData":[TD([[makeQuery(id+"F0.imprint","IMPRINT",EDGE,{"derivedFrom":subQ0}),1.0]])]});}
            var Q17;
            Q17=makeQuery(id+"F0.imprint","IMPRINT",FACE,{"disambiguationData":[TD([[makeQuery(id+"F0.imprint","IMPRINT",EDGE,{"derivedFrom":sQuery(id+"F0.wireOp",EDGE,"E201.MirrorCS")}),-1.0]])]});
            var Q18;
            {var subQ1=sQuery(id+"F0.wireOp",EDGE,"E201.MirrorCS");Q18=makeQuery(id+"F0.imprint","IMPRINT",FACE,{"disambiguationData":[TD([[makeQuery(id+"F0.imprint","IMPRINT",EDGE,{"derivedFrom":subQ1}),1.0]])]});}
            var Q19;
            Q19=makeQuery(id+"F0.imprint","IMPRINT",FACE,{"disambiguationData":[TD([[makeQuery(id+"F0.imprint","IMPRINT",EDGE,{"derivedFrom":sQuery(id+"F0.wireOp",EDGE,"E86.MirrorC")}),1.0]])]});
            extrude(context, id + "F1", {"entities" : qUnion([Q0, Q1, Q2, Q3, Q4, Q5, Q6, Q7, Q8, Q9, Q10, Q11, Q12, Q13, Q14, Q15, Q16, Q17, Q18, Q19]), "depth" : 4 * mm, "offsetDistance" : 25 * mm});
        }
        {
            var Q0;
            Q0=makeQuery(id+"F1.opExtrude","SWEPT_EDGE",EDGE,{"disambiguationData":[OSD([sQuery(id+"F0.wireOp",EDGE,"E69.bottom"),sQuery(id+"F0.wireOp",EDGE,"E84.top"),sQuery(id+"F0.wireOp",EDGE,"E84.right")])]});
            var Q1;
            Q1=makeQuery(id+"F1.opExtrude","SWEPT_EDGE",EDGE,{"disambiguationData":[OSD([sQuery(id+"F0.wireOp",EDGE,"E35.top"),sQuery(id+"F0.wireOp",EDGE,"E35.right")])]});
            var Q2;
            Q2=makeQuery(id+"F1.opExtrude","SWEPT_EDGE",EDGE,{"disambiguationData":[OSD([sQuery(id+"F0.wireOp",EDGE,"E96.MirrorCS"),sQuery(id+"F0.wireOp",EDGE,"E97.MirrorCS")])]});
            var Q3;
            Q3=makeQuery(id+"F1.opExtrude","SWEPT_EDGE",EDGE,{"disambiguationData":[OSD([sQuery(id+"F0.wireOp",EDGE,"E64.MirrorCS"),sQuery(id+"F0.wireOp",EDGE,"E61.MirrorCS")])]});
            fillet(context, id + "F2", {"entities" : qUnion([Q0, Q1, Q2, Q3]), "radius" : 7 * mm, "tangentPropagation" : true, "allowEdgeOverflow" : false});
        }
    });
